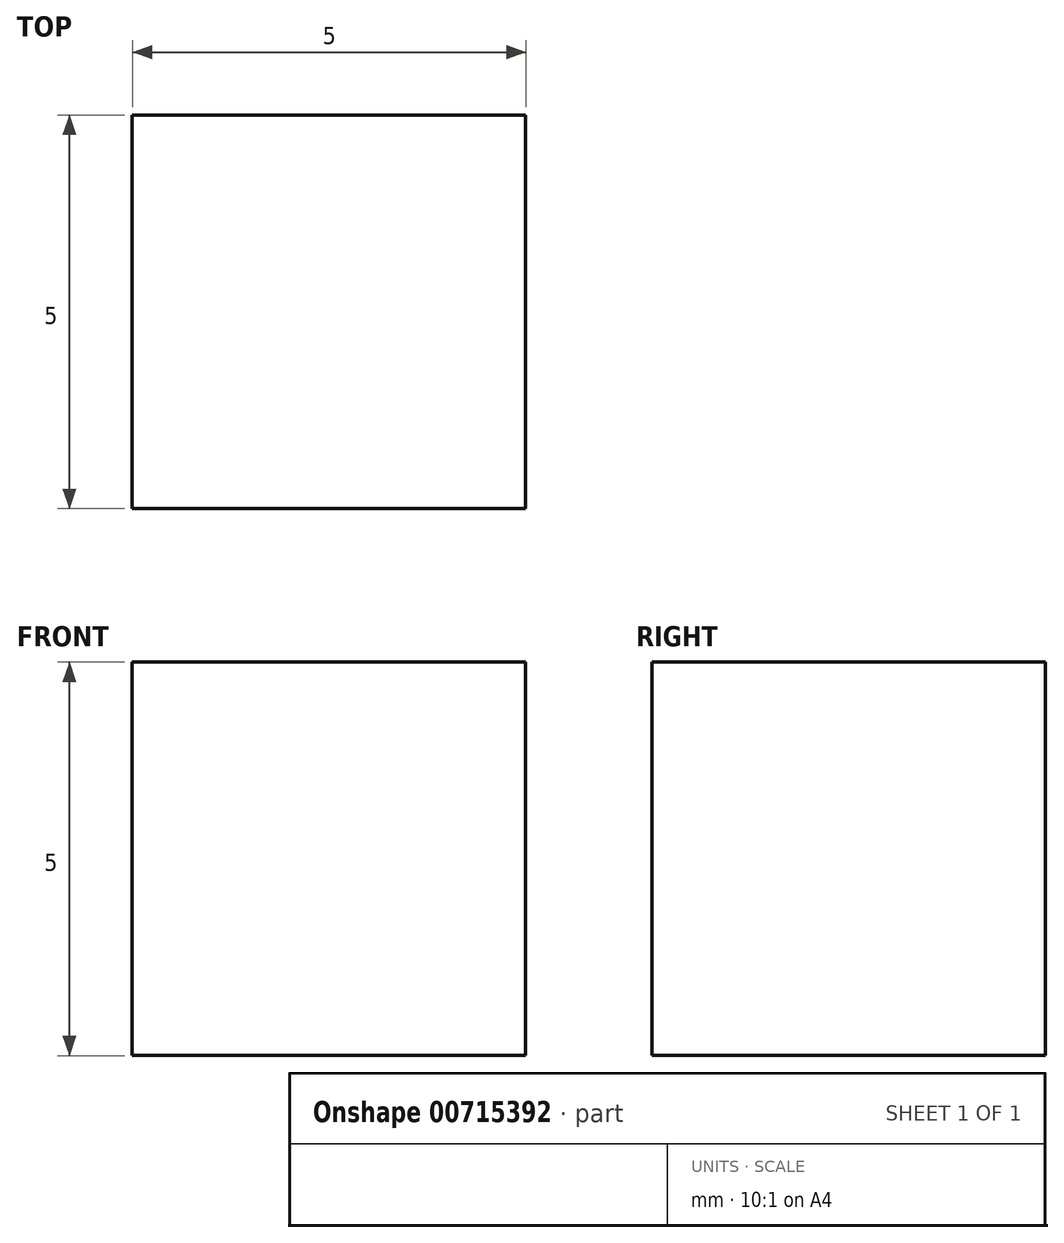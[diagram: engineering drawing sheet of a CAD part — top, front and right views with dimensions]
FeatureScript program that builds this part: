
annotation { "Feature Type Name" : "Feature", "Feature Type Description" : "" }
export const myFeature = defineFeature(function(context is Context, id is Id, definition is map)
    precondition{}
    {
        {
            assignVariable(context, id + "F0", {"name" : "X", "anyValue" : 5 * mm});
        }
        {
            var Q0;
            Q0=qCreatedBy(makeId("Front.planeOp"),FACE);
            var sketch = newSketch(context, id + "F1", { "sketchPlane" : qUnion([Q0])});
            skLineSegment(sketch, "E0", {"start": v(-2.42, 2.33) * mm, "end": v(2.58, 2.33) * mm});
            skLineSegment(sketch, "E1", {"start": v(2.58, 2.33) * mm, "end": v(2.58, -2.67) * mm});
            skLineSegment(sketch, "E2", {"start": v(2.58, -2.67) * mm, "end": v(-2.42, -2.67) * mm});
            skLineSegment(sketch, "E3", {"start": v(-2.42, -2.67) * mm, "end": v(-2.42, 2.33) * mm});
            skSolve(sketch);
        }
        {
            var Q0;
            Q0 = qSketchRegion(id + "F1", true);
            extrude(context, id + "F2", {"entities" : qUnion([Q0]), "depth" : getVariable(context, 'X'), "offsetDistance" : 25.4 * mm});
        }
    });
